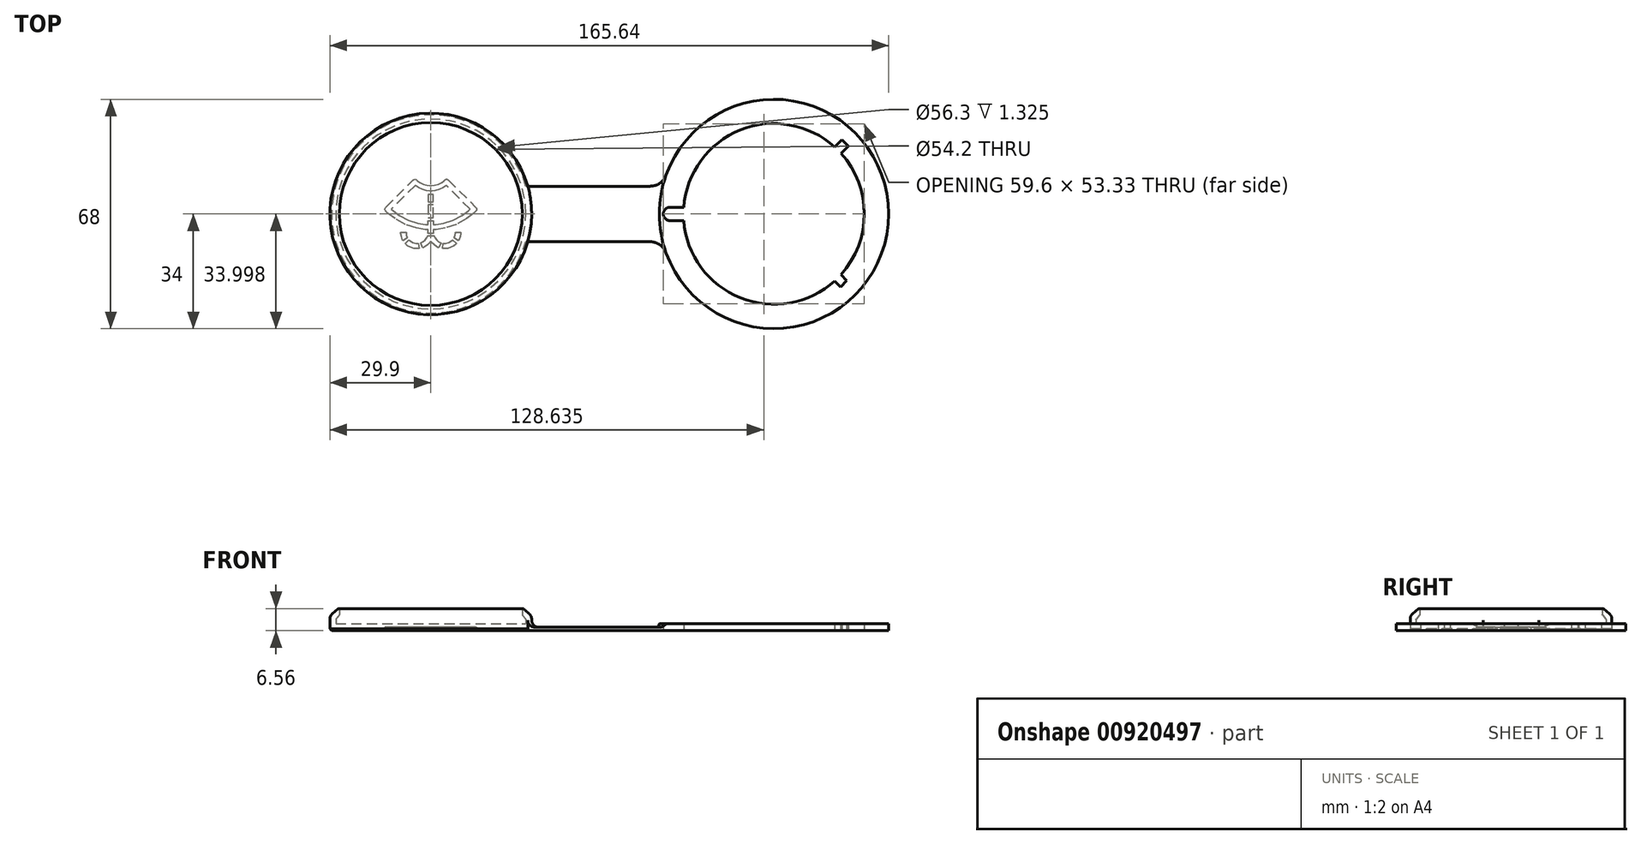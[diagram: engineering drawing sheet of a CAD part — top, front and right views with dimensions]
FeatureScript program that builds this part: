
annotation { "Feature Type Name" : "Feature", "Feature Type Description" : "" }
export const myFeature = defineFeature(function(context is Context, id is Id, definition is map)
    precondition{}
    {
        {
            var Q0;
            Q0=qCreatedBy(makeId("Front.planeOp"),FACE);
            var sketch = newSketch(context, id + "F0", { "sketchPlane" : qUnion([Q0])});
            skLineSegment(sketch, "E0.bottom", {"start": v(0, 0) * mm, "end": v(-29.9, 0) * mm});
            skLineSegment(sketch, "E0.top", {"start": v(0, 2) * mm, "end": v(-28.15, 2) * mm});
            skLineSegment(sketch, "E0.left", {"start": v(0, 0) * mm, "end": v(0, 2) * mm});
            skLineSegment(sketch, "E0.right", {"start": v(-29.9, 0) * mm, "end": v(-29.9, 2) * mm});
            skLineSegment(sketch, "E1", {"start": v(-29.9, 2) * mm, "end": v(-29.9, 4.4) * mm});
            skLineSegment(sketch, "E2", {"start": v(-29.9, 4.4) * mm, "end": v(-27.1, 6.8) * mm});
            skLineSegment(sketch, "E3", {"start": v(-27.1, 6.8) * mm, "end": v(-27.1, 4.6) * mm});
            skLineSegment(sketch, "E4", {"start": v(-28.15, 3.4) * mm, "end": v(-28.15, 2) * mm});
            skLineSegment(sketch, "E5", {"start": v(-28.15, 3.4) * mm, "end": v(-27.1, 4.6) * mm});
            skSolve(sketch);
        }
        {
            var Q0;
            Q0=makeQuery(id+"F0.imprint","IMPRINT",FACE,{"disambiguationData":[TD([[makeQuery(id+"F0.imprint","IMPRINT",EDGE,{"derivedFrom":sQuery(id+"F0.wireOp",EDGE,"E0.bottom")}),-1.0]])]});
            var Q1;
            Q1=sQuery(id+"F0.wireOp",EDGE,"E0.left");
            revolve(context, id + "F1", {"surfaceOperationType" : NewSurfaceOperationType.NEW, "entities" : qUnion([Q0]), "axis" : qUnion([Q1]), "revolveType" : RevolveType.FULL});
        }
        {
            var Q0;
            Q0=makeQuery(id+"F1.opRevolve","SWEPT_EDGE",EDGE,{"disambiguationData":[OSD([sQuery(id+"F0.wireOp",EDGE,"E2"),sQuery(id+"F0.wireOp",EDGE,"E3")])]});
            var Q1;
            Q1=makeQuery(id+"F1.opRevolve","SWEPT_EDGE",EDGE,{"disambiguationData":[OSD([sQuery(id+"F0.wireOp",EDGE,"E3"),sQuery(id+"F0.wireOp",EDGE,"E5")])]});
            var Q2;
            Q2=makeQuery(id+"F1.opRevolve","SWEPT_EDGE",EDGE,{"disambiguationData":[OSD([sQuery(id+"F0.wireOp",EDGE,"E4"),sQuery(id+"F0.wireOp",EDGE,"E5")])]});
            fillet(context, id + "F2", {"entities" : qUnion([Q0, Q1, Q2]), "radius" : 0.2 * mm, "tangentPropagation" : true, "allowEdgeOverflow" : false});
        }
        {
            var Q0;
            Q0=makeQuery(id+"F1.opRevolve","SWEPT_EDGE",EDGE,{"disambiguationData":[OSD([sQuery(id+"F0.wireOp",EDGE,"E1"),sQuery(id+"F0.wireOp",EDGE,"E2")])]});
            fillet(context, id + "F3", {"entities" : qUnion([Q0]), "radius" : 2 * mm, "tangentPropagation" : true, "allowEdgeOverflow" : false});
        }
        {
            var Q0;
            Q0=makeQuery(id+"F1.opRevolve","SWEPT_EDGE",EDGE,{"disambiguationData":[OSD([sQuery(id+"F0.wireOp",EDGE,"E0.bottom"),sQuery(id+"F0.wireOp",EDGE,"E0.right")])]});
            chamfer(context, id + "F4", {"entities" : qUnion([Q0]), "width" : 0.5 * mm, "tangentPropagation" : true});
        }
        {
            var Q0;
            Q0=makeQuery(id+"F1.opRevolve","SWEPT_FACE",FACE,{"disambiguationData":[OSD([sQuery(id+"F0.wireOp",EDGE,"E0.bottom")])]});
            var sketch = newSketch(context, id + "F5", { "sketchPlane" : qUnion([Q0])});
            skLineSegment(sketch, "E6", {"start": v(-6.89, 7.11) * mm, "end": v(-8.24, 7.9) * mm});
            skLineSegment(sketch, "E7", {"start": v(-8.24, 7.9) * mm, "end": v(-8.35, 7.72) * mm});
            skLineSegment(sketch, "E8", {"start": v(-8.35, 7.72) * mm, "end": v(-8.73, 6.73) * mm});
            skLineSegment(sketch, "E9", {"start": v(-8.73, 6.73) * mm, "end": v(-8.9, 5.79) * mm});
            skLineSegment(sketch, "E10", {"start": v(-8.9, 5.79) * mm, "end": v(-8.9, 5.47) * mm});
            skLineSegment(sketch, "E11", {"start": v(-8.9, 5.47) * mm, "end": v(-7.33, 5.47) * mm});
            skLineSegment(sketch, "E12", {"start": v(-7.33, 5.47) * mm, "end": v(-7.33, 5.68) * mm});
            skLineSegment(sketch, "E13", {"start": v(-7.33, 5.68) * mm, "end": v(-7.22, 6.32) * mm});
            skLineSegment(sketch, "E14", {"start": v(-7.22, 6.32) * mm, "end": v(-6.96, 7) * mm});
            skLineSegment(sketch, "E15", {"start": v(-6.96, 7) * mm, "end": v(-6.89, 7.11) * mm});
            skLineSegment(sketch, "E16", {"start": v(-4.06, 8.74) * mm, "end": v(-3.96, 8.74) * mm});
            skLineSegment(sketch, "E17", {"start": v(-3.96, 8.74) * mm, "end": v(-3.71, 8.73) * mm});
            skLineSegment(sketch, "E18", {"start": v(-3.71, 8.73) * mm, "end": v(-3.68, 8.72) * mm});
            skLineSegment(sketch, "E19", {"start": v(-3.68, 8.72) * mm, "end": v(-3.5, 10.28) * mm});
            skLineSegment(sketch, "E20", {"start": v(-3.5, 10.28) * mm, "end": v(-3.55, 10.28) * mm});
            skLineSegment(sketch, "E21", {"start": v(-3.55, 10.28) * mm, "end": v(-3.93, 10.3) * mm});
            skLineSegment(sketch, "E22", {"start": v(-3.93, 10.3) * mm, "end": v(-4.06, 10.3) * mm});
            skLineSegment(sketch, "E23", {"start": v(-4.06, 10.3) * mm, "end": v(-4.3, 10.3) * mm});
            skLineSegment(sketch, "E24", {"start": v(-4.3, 10.3) * mm, "end": v(-5.04, 10.2) * mm});
            skLineSegment(sketch, "E25", {"start": v(-5.04, 10.2) * mm, "end": v(-5.98, 9.9) * mm});
            skLineSegment(sketch, "E26", {"start": v(-5.98, 9.9) * mm, "end": v(-6.83, 9.43) * mm});
            skLineSegment(sketch, "E27", {"start": v(-6.83, 9.43) * mm, "end": v(-7.41, 8.96) * mm});
            skLineSegment(sketch, "E28", {"start": v(-7.41, 8.96) * mm, "end": v(-7.58, 8.78) * mm});
            skLineSegment(sketch, "E29", {"start": v(-7.58, 8.78) * mm, "end": v(-6.44, 7.71) * mm});
            skLineSegment(sketch, "E30", {"start": v(-6.44, 7.71) * mm, "end": v(-6.29, 7.88) * mm});
            skLineSegment(sketch, "E31", {"start": v(-6.29, 7.88) * mm, "end": v(-5.36, 8.48) * mm});
            skLineSegment(sketch, "E32", {"start": v(-5.36, 8.48) * mm, "end": v(-4.38, 8.74) * mm});
            skLineSegment(sketch, "E33", {"start": v(-4.38, 8.74) * mm, "end": v(-4.06, 8.74) * mm});
            skLineSegment(sketch, "E34", {"start": v(-0.92, 6.43) * mm, "end": v(0.92, 6.43) * mm});
            skLineSegment(sketch, "E35", {"start": v(0.92, 6.43) * mm, "end": v(0.98, 6.61) * mm});
            skLineSegment(sketch, "E36", {"start": v(0.98, 6.61) * mm, "end": v(1.23, 7.13) * mm});
            skLineSegment(sketch, "E37", {"start": v(1.23, 7.13) * mm, "end": v(1.7, 7.73) * mm});
            skLineSegment(sketch, "E38", {"start": v(1.7, 7.73) * mm, "end": v(2.27, 8.22) * mm});
            skLineSegment(sketch, "E39", {"start": v(2.27, 8.22) * mm, "end": v(2.78, 8.5) * mm});
            skLineSegment(sketch, "E40", {"start": v(2.78, 8.5) * mm, "end": v(2.96, 8.56) * mm});
            skLineSegment(sketch, "E41", {"start": v(2.96, 8.56) * mm, "end": v(2.43, 10.03) * mm});
            skLineSegment(sketch, "E42", {"start": v(2.43, 10.03) * mm, "end": v(2.18, 9.94) * mm});
            skLineSegment(sketch, "E43", {"start": v(2.18, 9.94) * mm, "end": v(1.05, 9.26) * mm});
            skLineSegment(sketch, "E44", {"start": v(1.05, 9.26) * mm, "end": v(0.14, 8.32) * mm});
            skLineSegment(sketch, "E45", {"start": v(0.14, 8.32) * mm, "end": v(0, 8.1) * mm});
            skLineSegment(sketch, "E46", {"start": v(0, 8.1) * mm, "end": v(-0.14, 8.32) * mm});
            skLineSegment(sketch, "E47", {"start": v(-0.14, 8.32) * mm, "end": v(-1.05, 9.26) * mm});
            skLineSegment(sketch, "E48", {"start": v(-1.05, 9.26) * mm, "end": v(-2.18, 9.94) * mm});
            skLineSegment(sketch, "E49", {"start": v(-2.18, 9.94) * mm, "end": v(-2.43, 10.03) * mm});
            skLineSegment(sketch, "E50", {"start": v(-2.43, 10.03) * mm, "end": v(-2.96, 8.56) * mm});
            skLineSegment(sketch, "E51", {"start": v(-2.96, 8.56) * mm, "end": v(-2.78, 8.5) * mm});
            skLineSegment(sketch, "E52", {"start": v(-2.78, 8.5) * mm, "end": v(-2.27, 8.22) * mm});
            skLineSegment(sketch, "E53", {"start": v(-2.27, 8.22) * mm, "end": v(-1.7, 7.73) * mm});
            skLineSegment(sketch, "E54", {"start": v(-1.7, 7.73) * mm, "end": v(-1.23, 7.13) * mm});
            skLineSegment(sketch, "E55", {"start": v(-1.23, 7.13) * mm, "end": v(-0.98, 6.61) * mm});
            skLineSegment(sketch, "E56", {"start": v(-0.98, 6.61) * mm, "end": v(-0.92, 6.43) * mm});
            skLineSegment(sketch, "E57", {"start": v(7.33, 5.47) * mm, "end": v(8.9, 5.47) * mm});
            skLineSegment(sketch, "E58", {"start": v(8.9, 5.47) * mm, "end": v(8.9, 5.79) * mm});
            skLineSegment(sketch, "E59", {"start": v(8.9, 5.79) * mm, "end": v(8.73, 6.73) * mm});
            skLineSegment(sketch, "E60", {"start": v(8.73, 6.73) * mm, "end": v(8.35, 7.72) * mm});
            skLineSegment(sketch, "E61", {"start": v(8.35, 7.72) * mm, "end": v(8.24, 7.9) * mm});
            skLineSegment(sketch, "E62", {"start": v(8.24, 7.9) * mm, "end": v(6.89, 7.11) * mm});
            skLineSegment(sketch, "E63", {"start": v(6.89, 7.11) * mm, "end": v(6.96, 7) * mm});
            skLineSegment(sketch, "E64", {"start": v(6.96, 7) * mm, "end": v(7.22, 6.32) * mm});
            skLineSegment(sketch, "E65", {"start": v(7.22, 6.32) * mm, "end": v(7.33, 5.68) * mm});
            skLineSegment(sketch, "E66", {"start": v(7.33, 5.68) * mm, "end": v(7.33, 5.47) * mm});
            skLineSegment(sketch, "E67", {"start": v(-0.78, 1.05) * mm, "end": v(0.78, 1.05) * mm});
            skLineSegment(sketch, "E68", {"start": v(0.78, 1.05) * mm, "end": v(0.78, -2.72) * mm});
            skLineSegment(sketch, "E69", {"start": v(0.78, -2.72) * mm, "end": v(-0.78, -2.72) * mm});
            skLineSegment(sketch, "E70", {"start": v(-0.78, -2.72) * mm, "end": v(-0.78, 1.05) * mm});
            skLineSegment(sketch, "E71", {"start": v(4.06, 8.74) * mm, "end": v(4.38, 8.74) * mm});
            skLineSegment(sketch, "E72", {"start": v(4.38, 8.74) * mm, "end": v(5.36, 8.48) * mm});
            skLineSegment(sketch, "E73", {"start": v(5.36, 8.48) * mm, "end": v(6.29, 7.88) * mm});
            skLineSegment(sketch, "E74", {"start": v(6.29, 7.88) * mm, "end": v(6.44, 7.71) * mm});
            skLineSegment(sketch, "E75", {"start": v(6.44, 7.71) * mm, "end": v(7.58, 8.78) * mm});
            skLineSegment(sketch, "E76", {"start": v(7.58, 8.78) * mm, "end": v(7.41, 8.96) * mm});
            skLineSegment(sketch, "E77", {"start": v(7.41, 8.96) * mm, "end": v(6.83, 9.43) * mm});
            skLineSegment(sketch, "E78", {"start": v(6.83, 9.43) * mm, "end": v(5.98, 9.9) * mm});
            skLineSegment(sketch, "E79", {"start": v(5.98, 9.9) * mm, "end": v(5.04, 10.2) * mm});
            skLineSegment(sketch, "E80", {"start": v(5.04, 10.2) * mm, "end": v(4.3, 10.3) * mm});
            skLineSegment(sketch, "E81", {"start": v(4.3, 10.3) * mm, "end": v(4.06, 10.3) * mm});
            skLineSegment(sketch, "E82", {"start": v(4.06, 10.3) * mm, "end": v(3.92, 10.3) * mm});
            skLineSegment(sketch, "E83", {"start": v(3.92, 10.3) * mm, "end": v(3.55, 10.28) * mm});
            skLineSegment(sketch, "E84", {"start": v(3.55, 10.28) * mm, "end": v(3.5, 10.28) * mm});
            skLineSegment(sketch, "E85", {"start": v(3.5, 10.28) * mm, "end": v(3.68, 8.72) * mm});
            skLineSegment(sketch, "E86", {"start": v(3.68, 8.72) * mm, "end": v(3.71, 8.73) * mm});
            skLineSegment(sketch, "E87", {"start": v(3.71, 8.73) * mm, "end": v(3.97, 8.74) * mm});
            skLineSegment(sketch, "E88", {"start": v(3.97, 8.74) * mm, "end": v(4.06, 8.74) * mm});
            skLineSegment(sketch, "E89", {"start": v(-0.78, -3.65) * mm, "end": v(0.78, -3.65) * mm});
            skLineSegment(sketch, "E90", {"start": v(0.78, -3.65) * mm, "end": v(0.78, -5.79) * mm});
            skLineSegment(sketch, "E91", {"start": v(0.78, -5.79) * mm, "end": v(-0.78, -5.79) * mm});
            skLineSegment(sketch, "E92", {"start": v(-0.78, -5.79) * mm, "end": v(-0.78, -3.65) * mm});
            skLineSegment(sketch, "E93", {"start": v(0.78, 4.67) * mm, "end": v(0.78, 5.8) * mm});
            skLineSegment(sketch, "E94", {"start": v(0.78, 5.8) * mm, "end": v(-0.78, 5.8) * mm});
            skLineSegment(sketch, "E95", {"start": v(-0.78, 5.8) * mm, "end": v(-0.78, 4.67) * mm});
            skLineSegment(sketch, "E96", {"start": v(-0.78, 4.67) * mm, "end": v(-1.66, 4.64) * mm});
            skLineSegment(sketch, "E97", {"start": v(-1.66, 4.64) * mm, "end": v(-4.27, 4.2) * mm});
            skLineSegment(sketch, "E98", {"start": v(-4.27, 4.2) * mm, "end": v(-7.58, 3.11) * mm});
            skLineSegment(sketch, "E99", {"start": v(-7.58, 3.11) * mm, "end": v(-10.63, 1.42) * mm});
            skLineSegment(sketch, "E100", {"start": v(-10.63, 1.42) * mm, "end": v(-12.73, -0.22) * mm});
            skLineSegment(sketch, "E101", {"start": v(-12.73, -0.22) * mm, "end": v(-13.35, -0.84) * mm});
            skLineSegment(sketch, "E102", {"start": v(-13.35, -0.84) * mm, "end": v(-13.39, -0.88) * mm});
            skLineSegment(sketch, "E103", {"start": v(-13.39, -0.88) * mm, "end": v(-13.52, -1.1) * mm});
            skLineSegment(sketch, "E104", {"start": v(-13.52, -1.1) * mm, "end": v(-13.58, -1.32) * mm});
            skLineSegment(sketch, "E105", {"start": v(-13.58, -1.32) * mm, "end": v(-13.58, -1.4) * mm});
            skLineSegment(sketch, "E106", {"start": v(-13.58, -1.4) * mm, "end": v(-13.58, -1.47) * mm});
            skLineSegment(sketch, "E107", {"start": v(-13.58, -1.47) * mm, "end": v(-13.52, -1.7) * mm});
            skLineSegment(sketch, "E108", {"start": v(-13.52, -1.7) * mm, "end": v(-13.39, -1.9) * mm});
            skLineSegment(sketch, "E109", {"start": v(-13.39, -1.9) * mm, "end": v(-13.35, -1.95) * mm});
            skLineSegment(sketch, "E110", {"start": v(-13.35, -1.95) * mm, "end": v(-5.22, -10.08) * mm});
            skLineSegment(sketch, "E111", {"start": v(-5.22, -10.08) * mm, "end": v(-5.16, -10.13) * mm});
            skLineSegment(sketch, "E112", {"start": v(-5.16, -10.13) * mm, "end": v(-4.96, -10.25) * mm});
            skLineSegment(sketch, "E113", {"start": v(-4.96, -10.25) * mm, "end": v(-4.66, -10.3) * mm});
            skLineSegment(sketch, "E114", {"start": v(-4.66, -10.3) * mm, "end": v(-4.37, -10.25) * mm});
            skLineSegment(sketch, "E115", {"start": v(-4.37, -10.25) * mm, "end": v(-4.17, -10.13) * mm});
            skLineSegment(sketch, "E116", {"start": v(-4.17, -10.13) * mm, "end": v(-4.11, -10.08) * mm});
            skLineSegment(sketch, "E117", {"start": v(-4.11, -10.08) * mm, "end": v(-3.91, -9.88) * mm});
            skLineSegment(sketch, "E118", {"start": v(-3.91, -9.88) * mm, "end": v(-3.22, -9.35) * mm});
            skLineSegment(sketch, "E119", {"start": v(-3.22, -9.35) * mm, "end": v(-2.23, -8.81) * mm});
            skLineSegment(sketch, "E120", {"start": v(-2.23, -8.81) * mm, "end": v(-1.14, -8.49) * mm});
            skLineSegment(sketch, "E121", {"start": v(-1.14, -8.49) * mm, "end": v(-0.29, -8.38) * mm});
            skLineSegment(sketch, "E122", {"start": v(-0.29, -8.38) * mm, "end": v(0, -8.38) * mm});
            skLineSegment(sketch, "E123", {"start": v(0, -8.38) * mm, "end": v(0.29, -8.38) * mm});
            skLineSegment(sketch, "E124", {"start": v(0.29, -8.38) * mm, "end": v(1.14, -8.49) * mm});
            skLineSegment(sketch, "E125", {"start": v(1.14, -8.49) * mm, "end": v(2.23, -8.81) * mm});
            skLineSegment(sketch, "E126", {"start": v(2.23, -8.81) * mm, "end": v(3.22, -9.35) * mm});
            skLineSegment(sketch, "E127", {"start": v(3.22, -9.35) * mm, "end": v(3.9, -9.88) * mm});
            skLineSegment(sketch, "E128", {"start": v(3.9, -9.88) * mm, "end": v(4.11, -10.08) * mm});
            skLineSegment(sketch, "E129", {"start": v(4.11, -10.08) * mm, "end": v(4.15, -10.12) * mm});
            skLineSegment(sketch, "E130", {"start": v(4.15, -10.12) * mm, "end": v(4.37, -10.25) * mm});
            skLineSegment(sketch, "E131", {"start": v(4.37, -10.25) * mm, "end": v(4.59, -10.3) * mm});
            skLineSegment(sketch, "E132", {"start": v(4.59, -10.3) * mm, "end": v(4.66, -10.3) * mm});
            skLineSegment(sketch, "E133", {"start": v(4.66, -10.3) * mm, "end": v(4.74, -10.3) * mm});
            skLineSegment(sketch, "E134", {"start": v(4.74, -10.3) * mm, "end": v(4.96, -10.25) * mm});
            skLineSegment(sketch, "E135", {"start": v(4.96, -10.25) * mm, "end": v(5.18, -10.12) * mm});
            skLineSegment(sketch, "E136", {"start": v(5.18, -10.12) * mm, "end": v(5.22, -10.08) * mm});
            skLineSegment(sketch, "E137", {"start": v(5.22, -10.08) * mm, "end": v(13.35, -1.95) * mm});
            skLineSegment(sketch, "E138", {"start": v(13.35, -1.95) * mm, "end": v(13.4, -1.9) * mm});
            skLineSegment(sketch, "E139", {"start": v(13.4, -1.9) * mm, "end": v(13.52, -1.69) * mm});
            skLineSegment(sketch, "E140", {"start": v(13.52, -1.69) * mm, "end": v(13.58, -1.4) * mm});
            skLineSegment(sketch, "E141", {"start": v(13.58, -1.4) * mm, "end": v(13.52, -1.1) * mm});
            skLineSegment(sketch, "E142", {"start": v(13.52, -1.1) * mm, "end": v(13.4, -0.9) * mm});
            skLineSegment(sketch, "E143", {"start": v(13.4, -0.9) * mm, "end": v(13.35, -0.84) * mm});
            skLineSegment(sketch, "E144", {"start": v(13.35, -0.84) * mm, "end": v(12.73, -0.22) * mm});
            skLineSegment(sketch, "E145", {"start": v(12.73, -0.22) * mm, "end": v(10.63, 1.42) * mm});
            skLineSegment(sketch, "E146", {"start": v(10.63, 1.42) * mm, "end": v(7.58, 3.11) * mm});
            skLineSegment(sketch, "E147", {"start": v(7.58, 3.11) * mm, "end": v(4.27, 4.2) * mm});
            skLineSegment(sketch, "E148", {"start": v(4.27, 4.2) * mm, "end": v(1.66, 4.64) * mm});
            skLineSegment(sketch, "E149", {"start": v(1.66, 4.64) * mm, "end": v(0.78, 4.67) * mm});
            skLineSegment(sketch, "E150", {"start": v(4.64, -8.45) * mm, "end": v(4.4, -8.25) * mm});
            skLineSegment(sketch, "E151", {"start": v(4.4, -8.25) * mm, "end": v(3.6, -7.75) * mm});
            skLineSegment(sketch, "E152", {"start": v(3.6, -7.75) * mm, "end": v(2.47, -7.23) * mm});
            skLineSegment(sketch, "E153", {"start": v(2.47, -7.23) * mm, "end": v(1.26, -6.92) * mm});
            skLineSegment(sketch, "E154", {"start": v(1.26, -6.92) * mm, "end": v(0.32, -6.81) * mm});
            skLineSegment(sketch, "E155", {"start": v(0.32, -6.81) * mm, "end": v(0, -6.81) * mm});
            skLineSegment(sketch, "E156", {"start": v(0, -6.81) * mm, "end": v(-0.32, -6.81) * mm});
            skLineSegment(sketch, "E157", {"start": v(-0.32, -6.81) * mm, "end": v(-1.26, -6.92) * mm});
            skLineSegment(sketch, "E158", {"start": v(-1.26, -6.92) * mm, "end": v(-2.47, -7.23) * mm});
            skLineSegment(sketch, "E159", {"start": v(-2.47, -7.23) * mm, "end": v(-3.6, -7.75) * mm});
            skLineSegment(sketch, "E160", {"start": v(-3.6, -7.75) * mm, "end": v(-4.4, -8.25) * mm});
            skLineSegment(sketch, "E161", {"start": v(-4.4, -8.25) * mm, "end": v(-4.64, -8.45) * mm});
            skLineSegment(sketch, "E162", {"start": v(-4.64, -8.45) * mm, "end": v(-11.68, -1.4) * mm});
            skLineSegment(sketch, "E163", {"start": v(-11.68, -1.4) * mm, "end": v(-11.12, -0.9) * mm});
            skLineSegment(sketch, "E164", {"start": v(-11.12, -0.9) * mm, "end": v(-9.28, 0.44) * mm});
            skLineSegment(sketch, "E165", {"start": v(-9.28, 0.44) * mm, "end": v(-6.63, 1.82) * mm});
            skLineSegment(sketch, "E166", {"start": v(-6.63, 1.82) * mm, "end": v(-3.78, 2.71) * mm});
            skLineSegment(sketch, "E167", {"start": v(-3.78, 2.71) * mm, "end": v(-1.53, 3.07) * mm});
            skLineSegment(sketch, "E168", {"start": v(-1.53, 3.07) * mm, "end": v(-0.78, 3.1) * mm});
            skLineSegment(sketch, "E169", {"start": v(-0.78, 3.1) * mm, "end": v(-0.78, 1.98) * mm});
            skLineSegment(sketch, "E170", {"start": v(-0.78, 1.98) * mm, "end": v(0.78, 1.98) * mm});
            skLineSegment(sketch, "E171", {"start": v(0.78, 1.98) * mm, "end": v(0.78, 3.1) * mm});
            skLineSegment(sketch, "E172", {"start": v(0.78, 3.1) * mm, "end": v(1.53, 3.07) * mm});
            skLineSegment(sketch, "E173", {"start": v(1.53, 3.07) * mm, "end": v(3.78, 2.71) * mm});
            skLineSegment(sketch, "E174", {"start": v(3.78, 2.71) * mm, "end": v(6.63, 1.82) * mm});
            skLineSegment(sketch, "E175", {"start": v(6.63, 1.82) * mm, "end": v(9.28, 0.44) * mm});
            skLineSegment(sketch, "E176", {"start": v(9.28, 0.44) * mm, "end": v(11.12, -0.9) * mm});
            skLineSegment(sketch, "E177", {"start": v(11.12, -0.9) * mm, "end": v(11.68, -1.4) * mm});
            skLineSegment(sketch, "E178", {"start": v(11.68, -1.4) * mm, "end": v(4.64, -8.45) * mm});
            skSolve(sketch);
        }
        {
            var Q0;
            Q0=makeQuery(id+"F5.imprint","IMPRINT",FACE,{"disambiguationData":[TD([[makeQuery(id+"F5.imprint","IMPRINT",EDGE,{"derivedFrom":sQuery(id+"F5.wireOp",EDGE,"E93")}),1.0]])]});
            var Q1;
            Q1=makeQuery(id+"F5.imprint","IMPRINT",FACE,{"disambiguationData":[TD([[makeQuery(id+"F5.imprint","IMPRINT",EDGE,{"derivedFrom":sQuery(id+"F5.wireOp",EDGE,"E89")}),-1.0]])]});
            var Q2;
            Q2=makeQuery(id+"F5.imprint","IMPRINT",FACE,{"disambiguationData":[TD([[makeQuery(id+"F5.imprint","IMPRINT",EDGE,{"derivedFrom":sQuery(id+"F5.wireOp",EDGE,"E67")}),-1.0]])]});
            var Q3;
            Q3=makeQuery(id+"F5.imprint","IMPRINT",FACE,{"disambiguationData":[TD([[makeQuery(id+"F5.imprint","IMPRINT",EDGE,{"derivedFrom":sQuery(id+"F5.wireOp",EDGE,"E34")}),1.0]])]});
            var Q4;
            Q4=makeQuery(id+"F5.imprint","IMPRINT",FACE,{"disambiguationData":[TD([[makeQuery(id+"F5.imprint","IMPRINT",EDGE,{"derivedFrom":sQuery(id+"F5.wireOp",EDGE,"E71")}),1.0]])]});
            var Q5;
            Q5=makeQuery(id+"F5.imprint","IMPRINT",FACE,{"disambiguationData":[TD([[makeQuery(id+"F5.imprint","IMPRINT",EDGE,{"derivedFrom":sQuery(id+"F5.wireOp",EDGE,"E57")}),1.0]])]});
            var Q6;
            Q6=makeQuery(id+"F5.imprint","IMPRINT",FACE,{"disambiguationData":[TD([[makeQuery(id+"F5.imprint","IMPRINT",EDGE,{"derivedFrom":sQuery(id+"F5.wireOp",EDGE,"E16")}),1.0]])]});
            var Q7;
            Q7=makeQuery(id+"F5.imprint","IMPRINT",FACE,{"disambiguationData":[TD([[makeQuery(id+"F5.imprint","IMPRINT",EDGE,{"derivedFrom":sQuery(id+"F5.wireOp",EDGE,"E6")}),1.0]])]});
            extrude(context, id + "F6", {"entities" : qUnion([Q0, Q1, Q2, Q3, Q4, Q5, Q6, Q7]), "operationType" : NewBodyOperationType.REMOVE, "oppositeDirection" : true, "depth" : 1 * mm, "offsetDistance" : 25 * mm});
        }
        {
            var Q0;
            Q0=qCreatedBy(makeId("Top.planeOp"),FACE);
            var sketch = newSketch(context, id + "F7", { "sketchPlane" : qUnion([Q0])});
            skCircle(sketch, "E179", {"center": v(101.74, 0) * mm, "radius": 34 * mm});
            skCircle(sketch, "E180", {"center": v(101.74, 0) * mm, "radius": 26.8 * mm});
            skLineSegment(sketch, "E181", {"start": v(67.74, 0) * mm, "end": v(29.9, 0) * mm, "construction": true});
            skLineSegment(sketch, "E182", {"start": v(68.75, 8.23) * mm, "end": v(28.75, 8.23) * mm});
            skLineSegment(sketch, "E183.MirrorCS", {"start": v(68.75, -8.23) * mm, "end": v(28.75, -8.23) * mm});
            skLineSegment(sketch, "E184", {"start": v(74.94, 0) * mm, "end": v(68.94, 0) * mm, "construction": true});
            skLineSegment(sketch, "E185", {"start": v(68.94, 0) * mm, "end": v(68.94, 0) * mm});
            skLineSegment(sketch, "E186", {"start": v(70.94, 2) * mm, "end": v(75, 2) * mm});
            skLineSegment(sketch, "E187.MirrorCS", {"start": v(70.94, -2) * mm, "end": v(75, -2) * mm});
            skLineSegment(sketch, "E188", {"start": v(101.74, 0) * mm, "end": v(125.78, 24.04) * mm, "construction": true});
            skLineSegment(sketch, "E189", {"start": v(101.74, 0) * mm, "end": v(135.74, 0) * mm, "construction": true});
            skLineSegment(sketch, "E190.MirrorCS", {"start": v(101.74, 0) * mm, "end": v(125.78, -24.04) * mm, "construction": true});
            skLineSegment(sketch, "E191", {"start": v(120.69, 18.95) * mm, "end": v(122.78, 21.05) * mm});
            skLineSegment(sketch, "E192", {"start": v(122.78, 21.05) * mm, "end": v(121.83, 22) * mm});
            skLineSegment(sketch, "E193", {"start": v(121.83, 22) * mm, "end": v(119.7, 19.88) * mm});
            skLineSegment(sketch, "E194.MirrorCS", {"start": v(123.74, 20.1) * mm, "end": v(121.62, 17.97) * mm});
            skLineSegment(sketch, "E195.MirrorCS", {"start": v(122.78, 21.05) * mm, "end": v(123.74, 20.1) * mm});
            skPoint(sketch, "E196.visualSharp", {"position": v(68.94, 2) * mm});
            skArc(sketch, "E196.filletArc", {"start": v(70.94, 2) * mm, "mid": v(69.52, 1.41) * mm, "end": v(68.94, 0) * mm});
            skPoint(sketch, "E197.visualSharp", {"position": v(68.94, -2) * mm});
            skArc(sketch, "E197.filletArc", {"start": v(68.94, 0) * mm, "mid": v(69.52, -1.41) * mm, "end": v(70.94, -2) * mm});
            skLineSegment(sketch, "E198", {"start": v(120.69, -18.95) * mm, "end": v(122.43, -20.7) * mm});
            skLineSegment(sketch, "E199", {"start": v(122.43, -20.7) * mm, "end": v(123.35, -19.78) * mm});
            skLineSegment(sketch, "E200", {"start": v(123.35, -19.78) * mm, "end": v(121.58, -18) * mm});
            skLineSegment(sketch, "E201.MirrorCS", {"start": v(121.51, -21.62) * mm, "end": v(119.74, -19.85) * mm});
            skLineSegment(sketch, "E202.MirrorCS", {"start": v(122.43, -20.7) * mm, "end": v(121.51, -21.62) * mm});
            skCircle(sketch, "E203.0", {"center": v(0, 0) * mm, "radius": 29.4 * mm});
            skLineSegment(sketch, "E204", {"start": v(28.75, -8.23) * mm, "end": v(28.23, -8.23) * mm});
            skLineSegment(sketch, "E205", {"start": v(28.75, 8.23) * mm, "end": v(28.23, 8.23) * mm});
            skSolve(sketch);
        }
        {
            var Q0;
            {var subQ2=sQuery(id+"F7.wireOp",EDGE,"E186");Q0=makeQuery(id+"F7.imprint","IMPRINT",FACE,{"disambiguationData":[TD([[makeQuery(id+"F7.imprint","IMPRINT",EDGE,{"derivedFrom":subQ2}),1.0]])]});}
            var Q1;
            {var subQ0=sQuery(id+"F7.wireOp",EDGE,"E182");Q1=makeQuery(id+"F7.imprint","IMPRINT",FACE,{"disambiguationData":[TD([[makeQuery(id+"F7.imprint","IMPRINT",EDGE,{"derivedFrom":subQ0}),1.0]])]});}
            var Q2;
            {var subQ2=sQuery(id+"F7.wireOp",EDGE,"E204");Q2=makeQuery(id+"F7.imprint","IMPRINT",FACE,{"disambiguationData":[TD([[makeQuery(id+"F7.imprint","IMPRINT",EDGE,{"derivedFrom":subQ2}),-1.0]])]});}
            extrude(context, id + "F8", {"entities" : qUnion([Q0, Q1, Q2]), "operationType" : NewBodyOperationType.ADD, "depth" : (0.35 * 3) * mm, "offsetDistance" : 25 * mm});
        }
        {
            var Q0;
            Q0=makeQuery(id+"F8.boolean.opBoolean","INTERSECT",EDGE,{"derivedFrom":[makeQuery(id+"F1.opRevolve","SWEPT_FACE",FACE,{"disambiguationData":[OSD([sQuery(id+"F0.wireOp",EDGE,"E0.right"),sQuery(id+"F0.wireOp",EDGE,"E1")])]}),makeQuery(id+"F8.opExtrude","CAP_FACE",FACE,{"disambiguationData":[OSD([sQuery(id+"F7.wireOp",EDGE,"E179"),sQuery(id+"F7.wireOp",EDGE,"E180"),sQuery(id+"F7.wireOp",EDGE,"E182"),sQuery(id+"F7.wireOp",EDGE,"E183.MirrorCS"),sQuery(id+"F7.wireOp",EDGE,"E186"),sQuery(id+"F7.wireOp",EDGE,"E187.MirrorCS"),sQuery(id+"F7.wireOp",EDGE,"E192"),sQuery(id+"F7.wireOp",EDGE,"E193"),sQuery(id+"F7.wireOp",EDGE,"E194.MirrorCS"),sQuery(id+"F7.wireOp",EDGE,"E195.MirrorCS"),sQuery(id+"F7.wireOp",EDGE,"E196.filletArc"),sQuery(id+"F7.wireOp",EDGE,"E197.filletArc"),sQuery(id+"F7.wireOp",EDGE,"E199"),sQuery(id+"F7.wireOp",EDGE,"E200"),sQuery(id+"F7.wireOp",EDGE,"E201.MirrorCS"),sQuery(id+"F7.wireOp",EDGE,"E202.MirrorCS"),sQuery(id+"F7.wireOp",EDGE,"E203.0"),sQuery(id+"F7.wireOp",EDGE,"E204"),sQuery(id+"F7.wireOp",EDGE,"E205")])],"isStart":false})]});
            fillet(context, id + "F9", {"entities" : qUnion([Q0]), "radius" : 2 * mm, "tangentPropagation" : true, "allowEdgeOverflow" : false});
        }
        {
            var Q0;
            Q0=makeQuery(id+"F8.opExtrude","SWEPT_EDGE",EDGE,{"disambiguationData":[OSD([sQuery(id+"F7.wireOp",EDGE,"E179"),sQuery(id+"F7.wireOp",EDGE,"E183.MirrorCS")])]});
            var Q1;
            Q1=makeQuery(id+"F8.opExtrude","SWEPT_EDGE",EDGE,{"disambiguationData":[OSD([sQuery(id+"F7.wireOp",EDGE,"E179"),sQuery(id+"F7.wireOp",EDGE,"E182")])]});
            fillet(context, id + "F10", {"entities" : qUnion([Q0, Q1]), "radius" : 5 * mm, "tangentPropagation" : true, "allowEdgeOverflow" : false});
        }
        {
            var Q0;
            {var subQ8=sQuery(id+"F7.wireOp",EDGE,"E186");Q0=makeQuery(id+"F7.imprint","IMPRINT",FACE,{"disambiguationData":[TD([[makeQuery(id+"F7.imprint","IMPRINT",EDGE,{"derivedFrom":subQ8}),1.0]])]});}
            extrude(context, id + "F11", {"entities" : qUnion([Q0]), "operationType" : NewBodyOperationType.ADD, "depth" : 2 * mm, "offsetDistance" : 25 * mm});
        }
        {
            var Q0;
            {var subQ0=sQuery(id+"F7.wireOp",EDGE,"E179");Q0=makeQuery(id+"F11.boolean.opBoolean","INTERSECT",EDGE,{"derivedFrom":[makeQuery(id+"F8.opExtrude","CAP_FACE",FACE,{"disambiguationData":[OSD([subQ0,sQuery(id+"F7.wireOp",EDGE,"E180"),sQuery(id+"F7.wireOp",EDGE,"E182"),sQuery(id+"F7.wireOp",EDGE,"E183.MirrorCS"),sQuery(id+"F7.wireOp",EDGE,"E186"),sQuery(id+"F7.wireOp",EDGE,"E187.MirrorCS"),sQuery(id+"F7.wireOp",EDGE,"E192"),sQuery(id+"F7.wireOp",EDGE,"E193"),sQuery(id+"F7.wireOp",EDGE,"E194.MirrorCS"),sQuery(id+"F7.wireOp",EDGE,"E195.MirrorCS"),sQuery(id+"F7.wireOp",EDGE,"E196.filletArc"),sQuery(id+"F7.wireOp",EDGE,"E197.filletArc"),sQuery(id+"F7.wireOp",EDGE,"E199"),sQuery(id+"F7.wireOp",EDGE,"E200"),sQuery(id+"F7.wireOp",EDGE,"E201.MirrorCS"),sQuery(id+"F7.wireOp",EDGE,"E202.MirrorCS"),sQuery(id+"F7.wireOp",EDGE,"E203.0"),sQuery(id+"F7.wireOp",EDGE,"E204"),sQuery(id+"F7.wireOp",EDGE,"E205")])],"isStart":false}),makeQuery(id+"F11.opExtrude","SWEPT_FACE",FACE,{"disambiguationData":[OSD([subQ0])]})]});}
            fillet(context, id + "F12", {"entities" : qUnion([Q0]), "tangentPropagation" : true, "radius" : 1 * mm, "defaultsChanged" : true, "vertexSettings" : [], "allowEdgeOverflow" : false});
        }
    });
